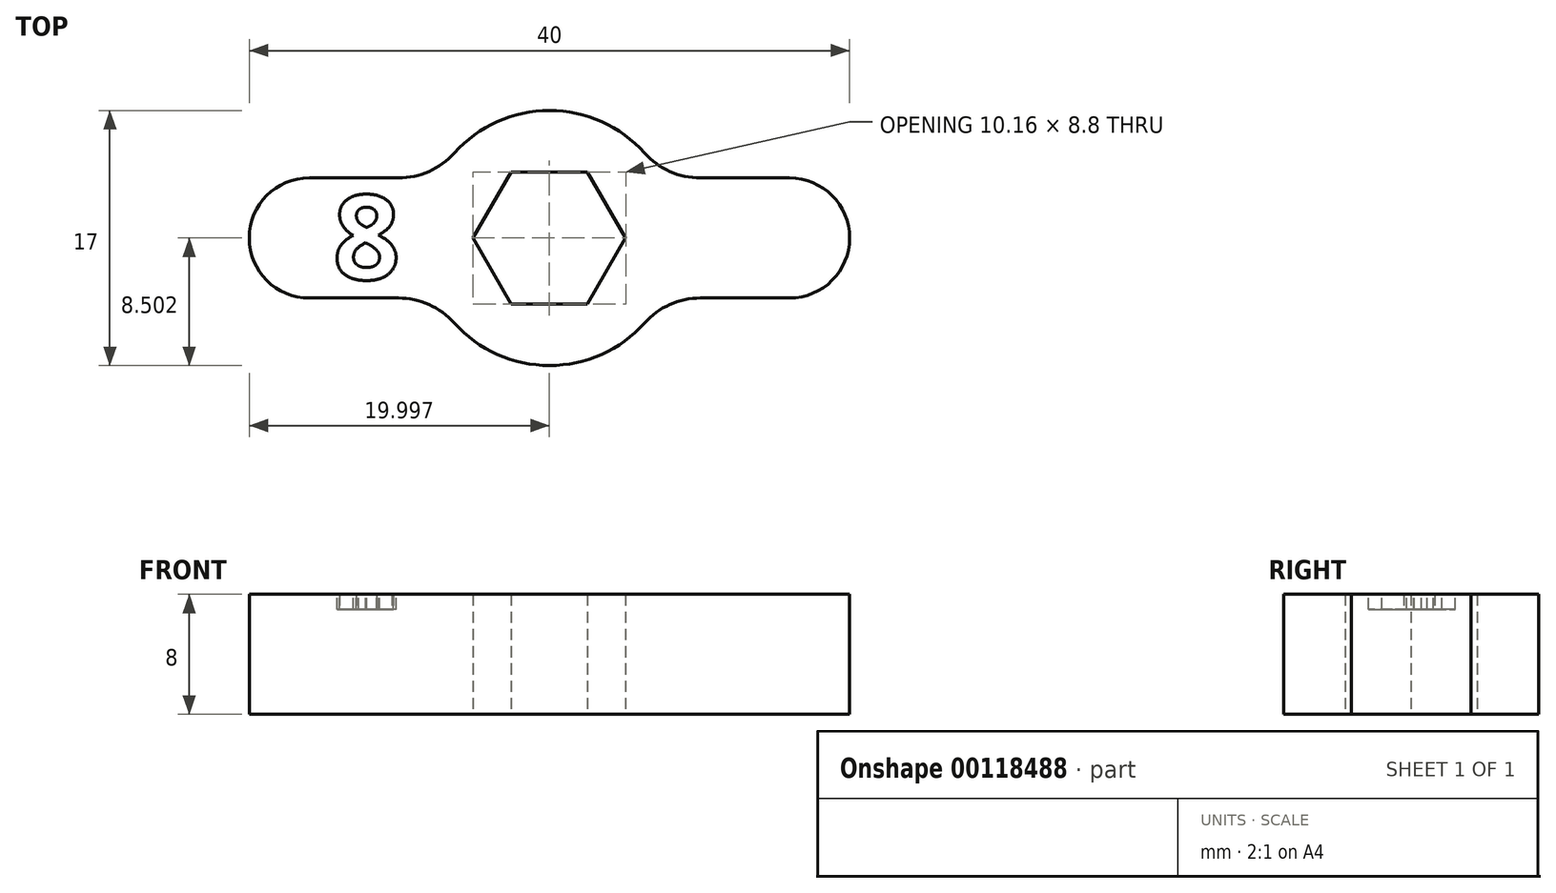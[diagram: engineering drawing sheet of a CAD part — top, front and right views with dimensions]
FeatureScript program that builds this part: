
annotation { "Feature Type Name" : "Feature", "Feature Type Description" : "" }
export const myFeature = defineFeature(function(context is Context, id is Id, definition is map)
    precondition{}
    {
        {
            var Q0;
            Q0=qCreatedBy(makeId("Top.planeOp"),FACE);
            var sketch = newSketch(context, id + "F0", { "sketchPlane" : qUnion([Q0])});
            skCircle(sketch, "E0.cCircle", {"center": v(-4.52, 3.54) * mm, "radius": 4.4 * mm, "construction": true});
            skLineSegment(sketch, "E0.0", {"start": v(0.56, 3.54) * mm, "end": v(-1.98, -0.86) * mm});
            skLineSegment(sketch, "E0.1", {"start": v(-1.98, -0.86) * mm, "end": v(-7.06, -0.86) * mm});
            skLineSegment(sketch, "E0.2", {"start": v(-7.06, -0.86) * mm, "end": v(-9.6, 3.54) * mm});
            skLineSegment(sketch, "E0.3", {"start": v(-9.6, 3.54) * mm, "end": v(-7.06, 7.94) * mm});
            skLineSegment(sketch, "E0.4", {"start": v(-7.06, 7.94) * mm, "end": v(-1.98, 7.94) * mm});
            skLineSegment(sketch, "E0.5", {"start": v(-1.98, 7.94) * mm, "end": v(0.56, 3.54) * mm});
            skPoint(sketch, "E0.0.midPoint", {"position": v(-0.71, 1.34) * mm});
            skCircle(sketch, "E1", {"center": v(-4.52, 3.54) * mm, "radius": 8.5 * mm});
            skLineSegment(sketch, "E2.bottom", {"start": v(2.98, 7.54) * mm, "end": v(11.48, 7.54) * mm});
            skLineSegment(sketch, "E2.top", {"start": v(2.98, -0.46) * mm, "end": v(11.48, -0.46) * mm});
            skArc(sketch, "E3", {"start": v(11.48, 7.54) * mm, "mid": v(15.48, 3.54) * mm, "end": v(11.48, -0.46) * mm});
            skLineSegment(sketch, "E4", {"start": v(-4.52, 15.76) * mm, "end": v(-4.52, -8.5) * mm, "construction": true});
            skLineSegment(sketch, "E5.MirrorCS", {"start": v(-12.02, 7.54) * mm, "end": v(-20.52, 7.54) * mm});
            skArc(sketch, "E6.MirrorCS", {"start": v(-20.52, 7.54) * mm, "mid": v(-24.52, 3.54) * mm, "end": v(-20.52, -0.46) * mm});
            skLineSegment(sketch, "E7.MirrorCS", {"start": v(-12.02, -0.46) * mm, "end": v(-20.52, -0.46) * mm});
            skLineSegment(sketch, "E8", {"start": v(-20.52, 3.54) * mm, "end": v(11.48, 3.54) * mm, "construction": true});
            skSolve(sketch);
        }
        {
            var Q0;
            {var subQ0=sQuery(id+"F0.wireOp",EDGE,"E5.MirrorCS");Q0=makeQuery(id+"F0.imprint","IMPRINT",FACE,{"disambiguationData":[TD([[makeQuery(id+"F0.imprint","IMPRINT",EDGE,{"derivedFrom":subQ0}),1.0]])]});}
            var Q1;
            Q1=makeQuery(id+"F0.imprint","IMPRINT",FACE,{"disambiguationData":[TD([[makeQuery(id+"F0.imprint","IMPRINT",EDGE,{"derivedFrom":sQuery(id+"F0.wireOp",EDGE,"E0.0")}),1.0]])]});
            var Q2;
            {var subQ0=sQuery(id+"F0.wireOp",EDGE,"E2.bottom");Q2=makeQuery(id+"F0.imprint","IMPRINT",FACE,{"disambiguationData":[TD([[makeQuery(id+"F0.imprint","IMPRINT",EDGE,{"derivedFrom":subQ0}),-1.0]])]});}
            extrude(context, id + "F1", {"entities" : qUnion([Q0, Q1, Q2]), "depth" : 8 * mm});
        }
        {
            var Q0;
            Q0=makeQuery(id+"F1.opExtrude","CAP_FACE",FACE,{"disambiguationData":[OSD([sQuery(id+"F0.wireOp",EDGE,"E0.0"),sQuery(id+"F0.wireOp",EDGE,"E0.1"),sQuery(id+"F0.wireOp",EDGE,"E0.2"),sQuery(id+"F0.wireOp",EDGE,"E0.3"),sQuery(id+"F0.wireOp",EDGE,"E0.4"),sQuery(id+"F0.wireOp",EDGE,"E0.5"),sQuery(id+"F0.wireOp",EDGE,"E1"),sQuery(id+"F0.wireOp",EDGE,"E2.bottom"),sQuery(id+"F0.wireOp",EDGE,"E2.top"),sQuery(id+"F0.wireOp",EDGE,"E3"),sQuery(id+"F0.wireOp",EDGE,"E5.MirrorCS"),sQuery(id+"F0.wireOp",EDGE,"E6.MirrorCS"),sQuery(id+"F0.wireOp",EDGE,"E7.MirrorCS")])],"isStart":false});
            var sketch = newSketch(context, id + "F2", { "sketchPlane" : qUnion([Q0])});
            skText(sketch, "E9", { "text": "8", "fontName": "OpenSans-Bold.ttf"});
            const initialGuessF2  = {"E9": [-0.01895, 0.00078, 1, 0, 0.00566]};
            skSetInitialGuess(sketch, initialGuessF2);
            skSolve(sketch);
        }
        {
            var Q0;
            Q0=qSketchRegion(id+"F2",true);
            extrude(context, id + "F3", {"entities" : qUnion([Q0]), "operationType" : NewBodyOperationType.REMOVE, "oppositeDirection" : true, "depth" : 1 * mm});
        }
        {
            var Q0;
            Q0=makeQuery(id+"F1.opExtrude","SWEPT_EDGE",EDGE,{"disambiguationData":[OSD([sQuery(id+"F0.wireOp",EDGE,"E1"),sQuery(id+"F0.wireOp",EDGE,"E2.top")])]});
            var Q1;
            Q1=makeQuery(id+"F1.opExtrude","SWEPT_EDGE",EDGE,{"disambiguationData":[OSD([sQuery(id+"F0.wireOp",EDGE,"E1"),sQuery(id+"F0.wireOp",EDGE,"E7.MirrorCS")])]});
            var Q2;
            Q2=makeQuery(id+"F1.opExtrude","SWEPT_EDGE",EDGE,{"disambiguationData":[OSD([sQuery(id+"F0.wireOp",EDGE,"E1"),sQuery(id+"F0.wireOp",EDGE,"E5.MirrorCS")])]});
            var Q3;
            Q3=makeQuery(id+"F1.opExtrude","SWEPT_EDGE",EDGE,{"disambiguationData":[OSD([sQuery(id+"F0.wireOp",EDGE,"E1"),sQuery(id+"F0.wireOp",EDGE,"E2.bottom")])]});
            fillet(context, id + "F4", {"entities" : qUnion([Q0, Q1, Q2, Q3]), "radius" : 5 * mm, "tangentPropagation" : true, "allowEdgeOverflow" : false});
        }
    });
